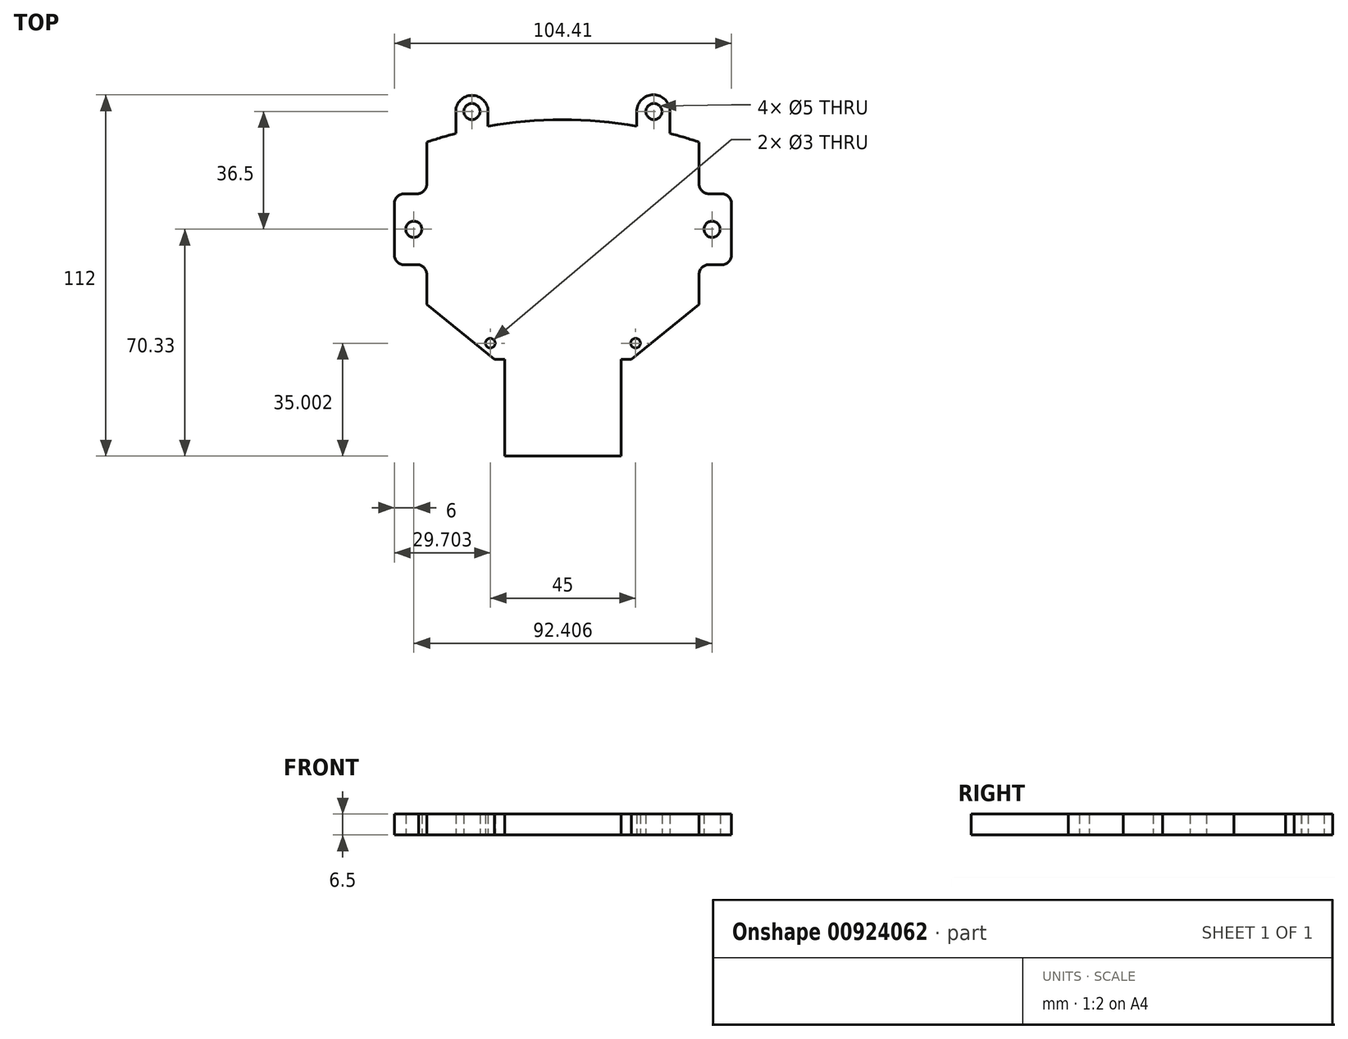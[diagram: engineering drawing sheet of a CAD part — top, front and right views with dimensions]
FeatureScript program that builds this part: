
annotation { "Feature Type Name" : "Feature", "Feature Type Description" : "" }
export const myFeature = defineFeature(function(context is Context, id is Id, definition is map)
    precondition{}
    {
        {
            var Q0;
            Q0=qCreatedBy(makeId("Top.planeOp"),FACE);
            var sketch = newSketch(context, id + "F0", { "sketchPlane" : qUnion([Q0])});
            skLineSegment(sketch, "E0", {"start": v(0, 0) * mm, "end": v(0, -22) * mm});
            skLineSegment(sketch, "E1", {"start": v(0, -22) * mm, "end": v(10, -22) * mm});
            skLineSegment(sketch, "E2", {"start": v(10, -22) * mm, "end": v(10, -34.3) * mm});
            skLineSegment(sketch, "E3", {"start": v(10, -34.3) * mm, "end": v(30.95, -51.33) * mm});
            skLineSegment(sketch, "E4", {"start": v(30.95, -51.33) * mm, "end": v(73.45, -51.33) * mm});
            skLineSegment(sketch, "E5", {"start": v(73.45, -51.33) * mm, "end": v(94.4, -34.3) * mm});
            skLineSegment(sketch, "E6", {"start": v(94.4, -34.3) * mm, "end": v(94.4, -22) * mm});
            skLineSegment(sketch, "E7", {"start": v(94.4, -22) * mm, "end": v(104.4, -22) * mm});
            skLineSegment(sketch, "E8", {"start": v(104.4, -22) * mm, "end": v(104.4, 0) * mm});
            skLineSegment(sketch, "E9", {"start": v(104.4, 0) * mm, "end": v(94.4, 0) * mm});
            skLineSegment(sketch, "E10", {"start": v(94.4, 0) * mm, "end": v(94.4, 16) * mm});
            skLineSegment(sketch, "E11", {"start": v(10, 16) * mm, "end": v(10, 0) * mm});
            skLineSegment(sketch, "E12", {"start": v(10, 0) * mm, "end": v(0, 0) * mm});
            skArc(sketch, "E13", {"start": v(94.4, 16) * mm, "mid": v(52.2, 23) * mm, "end": v(10, 16) * mm});
            skCircle(sketch, "E14", {"center": v(98.4, -11) * mm, "radius": 2.5 * mm});
            skCircle(sketch, "E15", {"center": v(6, -11) * mm, "radius": 2.5 * mm});
            skLineSegment(sketch, "E16", {"start": v(34.2, -51.33) * mm, "end": v(34.2, -81.33) * mm});
            skLineSegment(sketch, "E17", {"start": v(34.2, -81.33) * mm, "end": v(70.2, -81.33) * mm});
            skLineSegment(sketch, "E18", {"start": v(70.2, -81.33) * mm, "end": v(70.2, -51.33) * mm});
            skCircle(sketch, "E19", {"center": v(80.4, 25.5) * mm, "radius": 2.5 * mm});
            skCircle(sketch, "E20", {"center": v(24, 25.5) * mm, "radius": 2.5 * mm});
            skLineSegment(sketch, "E21", {"start": v(29, 25.5) * mm, "end": v(29, 20.92) * mm});
            skLineSegment(sketch, "E22", {"start": v(19, 25.5) * mm, "end": v(19, 18.71) * mm});
            skArc(sketch, "E23", {"start": v(29, 25.5) * mm, "mid": v(24, 30.5) * mm, "end": v(19, 25.5) * mm});
            skLineSegment(sketch, "E24", {"start": v(75.06, 25.5) * mm, "end": v(75.06, 20.99) * mm});
            skLineSegment(sketch, "E25", {"start": v(85.4, 25.5) * mm, "end": v(85.4, 18.71) * mm});
            skArc(sketch, "E26", {"start": v(85.4, 25.5) * mm, "mid": v(80.24, 30.67) * mm, "end": v(75.06, 25.5) * mm});
            skPoint(sketch, "E27", {"position": v(0, -3) * mm});
            skPoint(sketch, "E28", {"position": v(0, -19) * mm});
            skPoint(sketch, "E29", {"position": v(10, -25) * mm});
            skPoint(sketch, "E30", {"position": v(10, 3) * mm});
            skPoint(sketch, "E31", {"position": v(94.4, 3) * mm});
            skPoint(sketch, "E32", {"position": v(104.4, -3) * mm});
            skPoint(sketch, "E33", {"position": v(104.4, -19) * mm});
            skPoint(sketch, "E34", {"position": v(94.4, -25) * mm});
            skPoint(sketch, "E35", {"position": v(7, 0) * mm});
            skPoint(sketch, "E36", {"position": v(3, 0) * mm});
            skPoint(sketch, "E37", {"position": v(3, -22) * mm});
            skPoint(sketch, "E38", {"position": v(7, -22) * mm});
            skPoint(sketch, "E39", {"position": v(97.4, 0) * mm});
            skPoint(sketch, "E40", {"position": v(101.4, 0) * mm});
            skPoint(sketch, "E41", {"position": v(101.4, -22) * mm});
            skPoint(sketch, "E42", {"position": v(97.4, -22) * mm});
            skArc(sketch, "E43", {"start": v(7, 0) * mm, "mid": v(9.12, 0.88) * mm, "end": v(10, 3) * mm});
            skArc(sketch, "E44", {"start": v(3, 0) * mm, "mid": v(0.88, -0.88) * mm, "end": v(0, -3) * mm});
            skArc(sketch, "E45", {"start": v(0, -19) * mm, "mid": v(0.88, -21.12) * mm, "end": v(3, -22) * mm});
            skArc(sketch, "E46", {"start": v(10, -25) * mm, "mid": v(9.28, -23.02) * mm, "end": v(7.43, -22) * mm});
            skArc(sketch, "E47", {"start": v(97.4, -22) * mm, "mid": v(95.29, -22.88) * mm, "end": v(94.4, -25) * mm});
            skArc(sketch, "E48", {"start": v(101.4, -22) * mm, "mid": v(103.53, -21.12) * mm, "end": v(104.4, -19) * mm});
            skArc(sketch, "E49", {"start": v(104.4, -3) * mm, "mid": v(103.53, -0.88) * mm, "end": v(101.4, 0) * mm});
            skArc(sketch, "E50", {"start": v(94.4, 3) * mm, "mid": v(95.29, 0.88) * mm, "end": v(97.4, 0) * mm});
            skCircle(sketch, "E51", {"center": v(29.7, -46.33) * mm, "radius": 1.5 * mm});
            skCircle(sketch, "E52", {"center": v(74.7, -46.33) * mm, "radius": 1.5 * mm});
            skPoint(sketch, "E53", {"position": v(52.2, -51.33) * mm});
            skSolve(sketch);
        }
        {
            var Q0;
            {var subQ0=sQuery(id+"F0.wireOp",EDGE,"E2");var subQ1=sQuery(id+"F0.wireOp",EDGE,"E1");var subQ2=makeQuery(id+"F0.imprint","INTERSECT",VERTEX,{"derivedFrom":[subQ1,subQ0]});Q0=makeQuery(id+"F0.imprint","IMPRINT",FACE,{"disambiguationData":[TD([[makeQuery(id+"F0.imprint","IMPRINT",EDGE,{"disambiguationData":[TD([[subQ2,1.0]])],"derivedFrom":subQ1}),-1.0]])]});}
            var Q1;
            {var subQ0=sQuery(id+"F0.wireOp",EDGE,"E16");Q1=makeQuery(id+"F0.imprint","IMPRINT",FACE,{"disambiguationData":[TD([[makeQuery(id+"F0.imprint","IMPRINT",EDGE,{"derivedFrom":subQ0}),1.0]])]});}
            var Q2;
            {var subQ3=sQuery(id+"F0.wireOp",EDGE,"E47");Q2=makeQuery(id+"F0.imprint","IMPRINT",FACE,{"disambiguationData":[TD([[makeQuery(id+"F0.imprint","IMPRINT",EDGE,{"derivedFrom":subQ3}),-1.0]])]});}
            var Q3;
            {var subQ3=sQuery(id+"F0.wireOp",EDGE,"E50");Q3=makeQuery(id+"F0.imprint","IMPRINT",FACE,{"disambiguationData":[TD([[makeQuery(id+"F0.imprint","IMPRINT",EDGE,{"derivedFrom":subQ3}),-1.0]])]});}
            var Q4;
            {var subQ3=sQuery(id+"F0.wireOp",EDGE,"E43");Q4=makeQuery(id+"F0.imprint","IMPRINT",FACE,{"disambiguationData":[TD([[makeQuery(id+"F0.imprint","IMPRINT",EDGE,{"derivedFrom":subQ3}),-1.0]])]});}
            var Q5;
            Q5=makeQuery(id+"F0.imprint","IMPRINT",FACE,{"disambiguationData":[TD([[makeQuery(id+"F0.imprint","IMPRINT",EDGE,{"derivedFrom":sQuery(id+"F0.wireOp",EDGE,"E19")}),-1.0]])]});
            var Q6;
            Q6=makeQuery(id+"F0.imprint","IMPRINT",FACE,{"disambiguationData":[TD([[makeQuery(id+"F0.imprint","IMPRINT",EDGE,{"derivedFrom":sQuery(id+"F0.wireOp",EDGE,"E20")}),-1.0]])]});
            var Q7;
            {var subQ35=sQuery(id+"F0.wireOp",EDGE,"E3");Q7=makeQuery(id+"F0.imprint","IMPRINT",FACE,{"disambiguationData":[TD([[makeQuery(id+"F0.imprint","IMPRINT",EDGE,{"derivedFrom":subQ35}),1.0]])]});}
            extrude(context, id + "F1", {"entities" : qUnion([Q0, Q1, Q2, Q3, Q4, Q5, Q6, Q7]), "depth" : 6.5 * mm, "offsetDistance" : 25 * mm});
        }
    });
